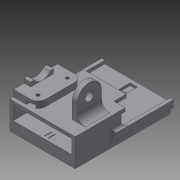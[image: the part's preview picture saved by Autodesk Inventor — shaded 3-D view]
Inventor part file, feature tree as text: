
AUTODESK INVENTOR PART (.ipt)
format: ipt  version: 2013 (Build 170138000, 138)  size: 469,504 bytes
history: native  units: mm
features: extrude x23, sketch x22, mirror x6, fillet x6, plane x2, hole x1, chamfer x1
ambient origin geometry x8: Origin, YZ Plane, XZ Plane, XY Plane, X Axis, Y Axis, Z Axis, Center Point
bodies: Solid1 (feature_tree)
feature tree (61):
  extrude  "Extrusion1"  Depth=6.35mm
  extrude  "Extrusion2"  Depth=10.0mm
  extrude  "Extrusion3"  Depth=8.5mm TaperAngle=0.0deg
  mirror  "Mirror1"
  extrude  "Extrusion4"  Depth=2.0mm TaperAngle=0.0deg
  mirror  "Mirror2"
  extrude  "Extrusion5"  Depth=2.0mm TaperAngle=0.0deg
  extrude  "Extrusion6"  Depth=12.5mm
  extrude  "Extrusion7"  Depth=12.5mm
  fillet  "Fillet1"  Radius=18.25mm
  extrude  "Extrusion8"  Depth=3.0mm
  plane  "Work Plane1"
  extrude  "Extrusion9"  Depth=5.0mm
  plane  "Work Plane2"
  mirror  "Mirror3"
  hole  "Hole1"  [1 undecoded]
  extrude  "Extrusion10"  Depth=7.5mm
  extrude  "Extrusion11"  Depth=7.5mm
  extrude  "Extrusion12"  Depth=27.0mm
  mirror  "Mirror4"
  fillet  "Fillet2"  Radius=4.0mm
  fillet  "Fillet3"  [1 undecoded]
  fillet  "Fillet4"  Radius=5.0mm
  extrude  "Extrusion13"  Depth=9.0mm
  sketch  "Sketch16"  dims[d45=4.5mm d46=9.0mm]
  extrude  "Extrusion14"  Depth=4.5mm
  extrude  "Extrusion15"  Depth=6.0mm
  extrude  "Extrusion17"  Depth=4.0mm TaperAngle=0.0deg
  extrude  "Extrusion16"  Depth=5.0mm TaperAngle=0.0deg
  chamfer  "Chamfer1"  Distance=2.0mm
  mirror  "Mirror5"
  extrude  "Extrusion18"  Depth=5.0mm
  extrude  "Extrusion19"  Depth=20.0mm TaperAngle=0.0deg
  fillet  "Fillet5"  Radius=37.0mm
  extrude  "Extrusion20"  Depth=40.0mm
  extrude  "Extrusion21"  Depth=1.5mm
  extrude  "Extrusion22"  Depth=4.5mm TaperAngle=0.0deg
  mirror  "Mirror6"
  fillet  "Fillet6"  Radius=4.5mm
  extrude  "Extrusion23"  Depth=8.0mm
  sketch  "Sketch1"  dims[d0=40.0mm d2=6.35mm]
  sketch  "Sketch2"  dims[d4=9.5mm d5=10.0mm]
  sketch  "Sketch4"  dims[d6=20.0mm d7=8.5mm d8=0.0mm]
  sketch  "Sketch5"  dims[d9=20.0mm d10=2.0mm d11=0.0mm]
  sketch  "Sketch6"  dims[d12=6.35mm d13=2.0mm d14=0.0mm]
  sketch  "Sketch7"  dims[d15=7.0mm d17=12.5mm]
  sketch  "Sketch9"  dims[d18=2.0mm d19=0.0mm d20=12.5mm d21=18.25mm d22=0.0mm]
  sketch  "Sketch10"  dims[d23=15.0mm d25=3.0mm]
  sketch  "Sketch11"  dims[d26=4.5mm d27=5.0mm]
  sketch  "Sketch12"  dims[d28=14.5mm d29=17.5mm d30=0.0mm]
  sketch  "Sketch13"  dims[d31=5.1mm d34=7.5mm]
  sketch  "Sketch14"  dims[d35=10.0mm d36=0.0mm d37=7.5mm]
  sketch  "Sketch15"  dims[d38=15.0mm d39=27.0mm d41=4.0mm d42=0.0mm d43=-2.0mm d44=5.0mm]
  sketch  "Sketch17"  dims[d47=2.0mm d48=0.0mm d49=4.5mm]
  sketch  "Sketch18"  dims[d50=18.0mm]
  sketch  "Sketch19"  dims[d51=2.013mm d52=6.0mm d53=4.0mm d54=2.0mm d55=90.0deg d56=4.0mm d57=20.594885mm d58=6.0mm]
  sketch  "Sketch20"  dims[d61=10.0mm d62=4.0mm d63=0.0mm]
  sketch  "Sketch21"  dims[d64=12.0mm d65=5.0mm d66=0.0mm d67=2.0mm d68=0.0mm]
  sketch  "Sketch23"  dims[d69=4.5mm d70=5.0mm]
  sketch  "Sketch24"  dims[d71=2.0mm d72=20.0mm d73=0.0mm d74=37.0mm]
  sketch  "Sketch25"  dims[d76=56.75mm d78=40.0mm d79=1.5mm d80=4.5mm d81=0.0mm d82=4.5mm d83=0.0mm d84=8.0mm d85=6.0mm d86=20.0mm d87=0.25mm d88=2.5mm d89=0.0mm d90=2.0mm d93=5.5mm d94=24.5mm d95=2.25mm d96=0.0mm d97=1.0mm d98=2.0mm d99=45.0deg d100=54.5mm d101=0.5mm d102=0.5mm d103=7.0mm d104=3.5mm d105=2.25mm d106=0.0mm d107=1.0mm d108=0.0mm d109=2.0mm d110=1.0mm d111=2.5mm d112=1.0mm d113=0.0mm d114=16.25mm d116=18.5mm d117=1.75mm d118=4.25mm d119=5.0mm d120=0.0mm d121=2.0mm d122=35.0mm d123=4.0mm d124=0.0mm d125=2.0mm d126=2.0mm d127=2.0mm d128=2.0mm d129=15.0mm d130=0.0mm]
note: 2 required parameter values undecoded (feature->parameter linkage not recoverable at this tier; creation-order binding heuristic only, values carry confidence <= 0.55)
